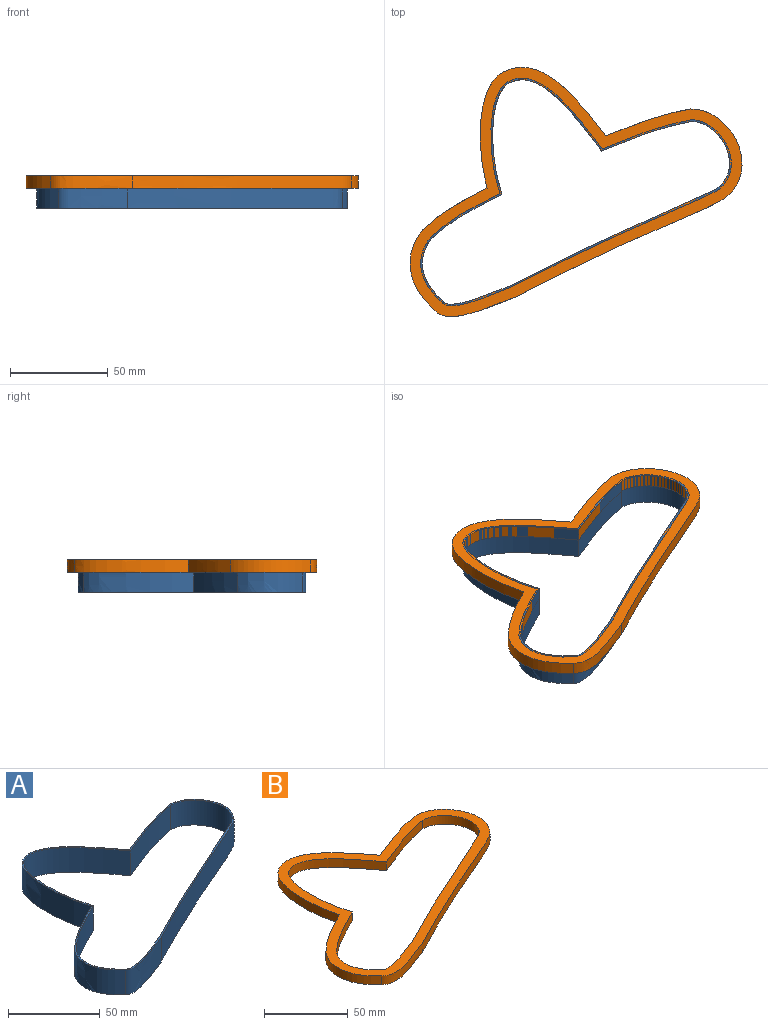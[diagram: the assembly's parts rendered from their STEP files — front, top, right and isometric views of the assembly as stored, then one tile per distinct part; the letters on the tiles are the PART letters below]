
ASSEMBLY  parts=2 mates=1
PART A: 18 faces, bbox 164.6x123.9x20.3 mm
  f0: plane 164.6x123.88mm, normal (0,0,1), area 402.6mm2, adj f2,f3,f4,f5,f6,f7,f8,f9
  f1: plane 164.6x123.88mm, normal (0,0,-1), area 402.2mm2, adj f2,f3,f4,f5,f6,f7,f8,f9
  f2: extruded ~56.46x16.51mm, area 970.7mm2, adj f0,f1,f3,f9
  f3: extruded ~35.46x22.35mm, area 695.2mm2, adj f0,f1,f2,f4
  f4: extruded ~33.34x16.51mm, area 627.9mm2, adj f0,f1,f3,f5
  f5: extruded ~35.54x16.51mm, area 620.6mm2, adj f0,f1,f4,f6
  f6: extruded ~109.58x54.26mm, area 2028.5mm2, adj f0,f1,f5,f7
  f7: extruded ~31.16x20.34mm, area 700mm2, adj f0,f1,f6,f8
  f8: extruded ~45.64x16.51mm, area 794.5mm2, adj f0,f1,f7,f9
  f9: extruded ~49.17x36.17mm, area 1072.6mm2, adj f0,f1,f2,f8
  f10: extruded ~56.2x16.51mm, area 964.9mm2, adj f0,f1,f11,f17
  f11: extruded ~35.88x22.5mm, area 702.4mm2, adj f0,f1,f10,f12
  f12: extruded ~32.11x16.51mm, area 605.4mm2, adj f0,f1,f11,f13
  f13: extruded ~34.53x16.51mm, area 602.5mm2, adj f0,f1,f12,f14
  f14: extruded ~109.21x53.92mm, area 2020.1mm2, adj f0,f1,f13,f15
  f15: extruded ~29.8x19.38mm, area 667.6mm2, adj f0,f1,f14,f16
  f16: extruded ~46x16.51mm, area 801mm2, adj f0,f1,f15,f17
  f17: extruded ~48.36x36.35mm, area 1061.2mm2, adj f0,f1,f10,f16
PART B: 18 faces, bbox 171.5x129.2x8.2 mm
  f0: plane 171.46x129.22mm, normal (0,0,1), area 2971.9mm2, adj f2,f3,f4,f5,f6,f7,f8,f9
  f1: plane 171.46x129.22mm, normal (0,0,-1), area 2971.5mm2, adj f2,f3,f4,f5,f6,f7,f8,f9
  f2: extruded ~58.01x9.92mm, area 387.4mm2, adj f0,f1,f3,f9
  f3: extruded ~32.96x21.5mm, area 251mm2, adj f0,f1,f2,f4
  f4: extruded ~40.97x12.62mm, area 295.2mm2, adj f0,f1,f3,f5
  f5: extruded ~41.69x10.22mm, area 280.8mm2, adj f0,f1,f4,f6
  f6: extruded ~111.91x56.34mm, area 800.3mm2, adj f0,f1,f5,f7
  f7: extruded ~39.49x26.22mm, area 345.9mm2, adj f0,f1,f6,f8
  f8: extruded ~43.41x13.72mm, area 289.8mm2, adj f0,f1,f7,f9
  f9: extruded ~54.19x34.97mm, area 439.9mm2, adj f0,f1,f2,f8
  f10: extruded ~56.2x7.31mm, area 371.1mm2, adj f0,f1,f11,f17
  f11: extruded ~35.88x22.5mm, area 270.2mm2, adj f0,f1,f10,f12
  f12: extruded ~32.11x10.72mm, area 232.8mm2, adj f0,f1,f11,f13
  f13: extruded ~34.53x9.61mm, area 231.7mm2, adj f0,f1,f12,f14
  f14: extruded ~109.21x53.92mm, area 777mm2, adj f0,f1,f13,f15
  f15: extruded ~29.8x19.38mm, area 256.8mm2, adj f0,f1,f14,f16
  f16: extruded ~46x15.1mm, area 308.1mm2, adj f0,f1,f15,f17
  f17: extruded ~48.36x36.35mm, area 408.1mm2, adj f0,f1,f10,f16
PLACE A t=(157.78,-5.02,-10.16)mm
PLACE B at identity
MATE fastened A.f0 <-> B.f0  axis (0,0,1) through (175.32,32.29,6.35)mm
